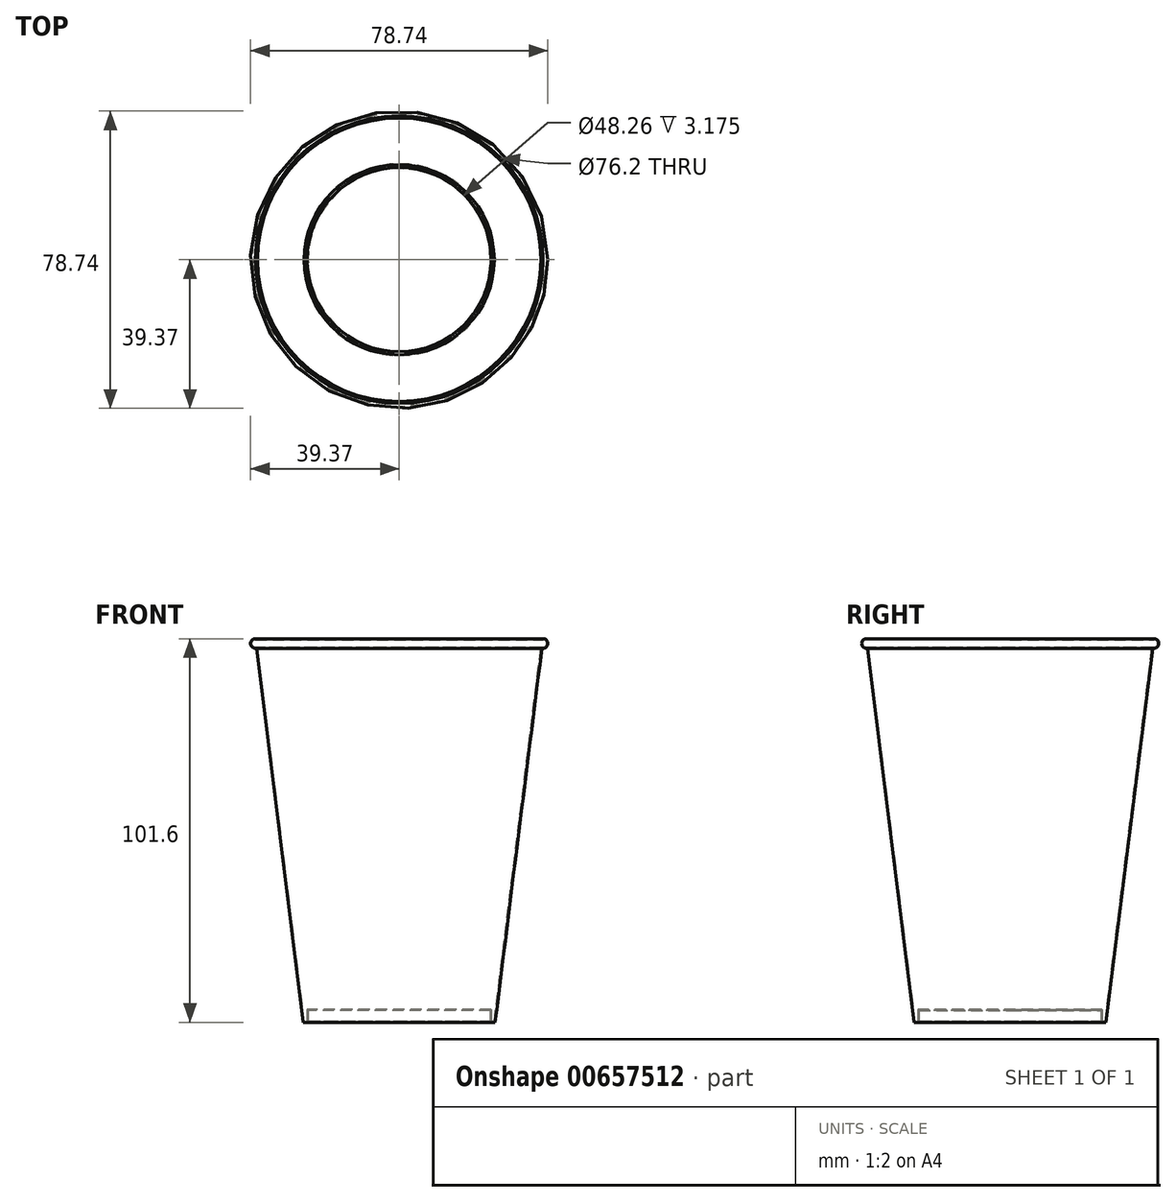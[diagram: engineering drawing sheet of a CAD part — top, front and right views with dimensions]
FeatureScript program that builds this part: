
annotation { "Feature Type Name" : "Feature", "Feature Type Description" : "" }
export const myFeature = defineFeature(function(context is Context, id is Id, definition is map)
    precondition{}
    {
        {
            var Q0;
            Q0=qCreatedBy(makeId("Top.planeOp"),FACE);
            var sketch = newSketch(context, id + "F0", { "sketchPlane" : qUnion([Q0])});
            skCircle(sketch, "E0", {"center": v(0, 0) * mm, "radius": 38.1 * mm});
            skSolve(sketch);
        }
        {
            var Q0;
            Q0=qCreatedBy(makeId("Top.planeOp"),FACE);
            cPlane(context, id + "F1", {"entities" : qUnion([Q0]), "cplaneType" : CPlaneType.OFFSET, "offset" : 101.6 * mm, "oppositeDirection" : true, "width" : 152.4 * mm, "height" : 152.4 * mm});
        }
        {
            var Q0;
            Q0=qCreatedBy(id+"F1.planeOp",FACE);
            var sketch = newSketch(context, id + "F2", { "sketchPlane" : qUnion([Q0])});
            skCircle(sketch, "E1", {"center": v(0, 0) * mm, "radius": 25.4 * mm});
            skSolve(sketch);
        }
        {
            var Q0;
            Q0=qCreatedBy(id+"F1.planeOp",FACE);
            var sketch = newSketch(context, id + "F3", { "sketchPlane" : qUnion([Q0])});
            skCircle(sketch, "E2", {"center": v(0, 0) * mm, "radius": 24.13 * mm});
            skSolve(sketch);
        }
        {
            var Q0;
            Q0=makeQuery(id+"F2.imprint","IMPRINT",FACE,{"disambiguationData":[TD([[makeQuery(id+"F2.imprint","IMPRINT",EDGE,{"derivedFrom":sQuery(id+"F2.wireOp",EDGE,"E1")}),1.0]])]});
            var Q1;
            Q1=makeQuery(id+"F0.imprint","IMPRINT",FACE,{"disambiguationData":[TD([[makeQuery(id+"F0.imprint","IMPRINT",EDGE,{"derivedFrom":sQuery(id+"F0.wireOp",EDGE,"E0")}),1.0]])]});
            loft(context, id + "F4", {"sheetProfilesArray" : [{ "sheetProfileEntities" : qUnion([Q0]) }, { "sheetProfileEntities" : qUnion([Q1]) }]});
        }
        {
            var Q0;
            Q0=makeQuery(id+"F3.imprint","IMPRINT",FACE,{"disambiguationData":[TD([[makeQuery(id+"F3.imprint","IMPRINT",EDGE,{"derivedFrom":sQuery(id+"F3.wireOp",EDGE,"E2")}),1.0]])]});
            extrude(context, id + "F5", {"entities" : qUnion([Q0]), "operationType" : NewBodyOperationType.REMOVE, "depth" : 3.17 * mm, "offsetDistance" : 25.4 * mm});
        }
        {
            var Q0;
            Q0=qCreatedBy(makeId("Top.planeOp"),FACE);
            var sketch = newSketch(context, id + "F6", { "sketchPlane" : qUnion([Q0])});
            skCircle(sketch, "E3", {"center": v(0, 0) * mm, "radius": 39.37 * mm});
            skSolve(sketch);
        }
        {
            var Q0;
            Q0=makeQuery(id+"F6.imprint","IMPRINT",FACE,{"disambiguationData":[TD([[makeQuery(id+"F6.imprint","IMPRINT",EDGE,{"derivedFrom":sQuery(id+"F6.wireOp",EDGE,"E3")}),1.0]])]});
            extrude(context, id + "F7", {"entities" : qUnion([Q0]), "operationType" : NewBodyOperationType.ADD, "oppositeDirection" : true, "depth" : 2.54 * mm, "offsetDistance" : 25.4 * mm});
        }
        {
            var Q0;
            Q0=makeQuery(id+"F7.opExtrude","CAP_EDGE",EDGE,{"disambiguationData":[OSD([sQuery(id+"F6.wireOp",EDGE,"E3")])],"isStart":false});
            var Q1;
            Q1=makeQuery(id+"F7.opExtrude","CAP_EDGE",EDGE,{"disambiguationData":[OSD([sQuery(id+"F6.wireOp",EDGE,"E3")])],"isStart":true});
            fillet(context, id + "F8", {"entities" : qUnion([Q0, Q1]), "radius" : 1.27 * mm, "tangentPropagation" : true, "allowEdgeOverflow" : false});
        }
        {
            var Q0;
            Q0=makeQuery(id+"F7.boolean.opBoolean","MERGE",FACE,{"derivedFrom":[makeQuery(id+"F4.opLoft","CAP_FACE",FACE,{"disambiguationData":[OSD([makeQuery(id+"F0.imprint","IMPRINT",FACE,{"disambiguationData":[TD([[makeQuery(id+"F0.imprint","IMPRINT",EDGE,{"derivedFrom":sQuery(id+"F0.wireOp",EDGE,"E0")}),1.0]])]})])],"isStart":true}),makeQuery(id+"F7.opExtrude","CAP_FACE",FACE,{"disambiguationData":[OSD([sQuery(id+"F6.wireOp",EDGE,"E3")])],"isStart":true})]});
            shell(context, id + "F9", {"entities" : qUnion([Q0]), "thickness" : 0.25 * mm});
        }
    });
